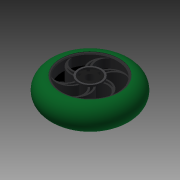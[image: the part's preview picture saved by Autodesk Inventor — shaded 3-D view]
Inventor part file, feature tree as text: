
AUTODESK INVENTOR PART (.ipt)
format: ipt  version: 2015 (Build 190159000, 159)  size: 857,088 bytes
history: native  units: in
note: dims shown in document units (in); Inventor stores cm internally (conversion verified against a paired STEP export)
features: sketch x14, extrude x11, mirror x6, sweep x1, chamfer x1, projected_geometry x1
ambient origin geometry x8: Origin, YZ Plane, XZ Plane, XY Plane, X Axis, Y Axis, Z Axis, Center Point
bodies: Solid1 (feature_tree)
feature tree (34):
  sweep  "Sweep1"
  sketch  "Sketch3"  dims[d18=0.0625in d19=0.0in d20=0.25in d21=0.0in]
  sketch  "Sketch6"  dims[d22=0.0625in d23=0.0in d24=0.0625in d25=0.0in]
  extrude  "Extrusion4"  Depth=1.75in
  extrude  "Extrusion5"  Depth=0.0625in TaperAngle=0.0deg
  extrude  "Extrusion6"  Depth=0.0625in TaperAngle=0.0deg
  mirror  "Mirror1"
  extrude  "Extrusion7"  Depth=0.24in TaperAngle=0.0deg
  mirror  "Mirror2"
  sketch  "Sketch11"  dims[d38=0.025in d39=0.125in d40=45.0deg d105=0.25in]
  extrude  "Extrusion8"  Depth=0.0625in TaperAngle=0.0deg
  extrude  "Extrusion9"  Depth=0.65in TaperAngle=0.0deg
  mirror  "Mirror3"
  extrude  "Extrusion10"  Depth=0.125in
  mirror  "Mirror4"
  extrude  "Extrusion11"  [1 undecoded]
  mirror  "Mirror5"
  extrude  "Extrusion12"  [1 undecoded]
  mirror  "Mirror6"
  extrude  "Extrusion13"  [1 undecoded]
  chamfer  "Chamfer1"  [1 undecoded]
  extrude  "Extrusion26"  [1 undecoded]
  sketch  "Sketch1"  dims[d0=2.5in d1=0.75in]
  sketch  "Sketch2"  dims[d2=0.0in d3=0.0in d4=1.75in]
  sketch  "Sketch7"  dims[d26=0.25in d27=0.0in d28=0.24in d29=0.0in]
  sketch  "Sketch9"  dims[d30=0.2in d31=0.0in d32=0.0625in d33=0.0in]
  sketch  "Sketch10"  dims[d34=0.05in d35=0.0in d36=0.65in d37=0.0in]
  sketch  "Sketch12"  dims[d106=1.0in d107=0.0in]
  sketch  "Sketch14"
  projected_geometry  "Projected Loop2"
  sketch  "Sketch15"
  sketch  "Sketch16"
  sketch  "Sketch18"
  sketch  "Sketch35"
note: 5 required parameter values undecoded (feature->parameter linkage not recoverable at this tier; creation-order binding heuristic only, values carry confidence <= 0.55)
